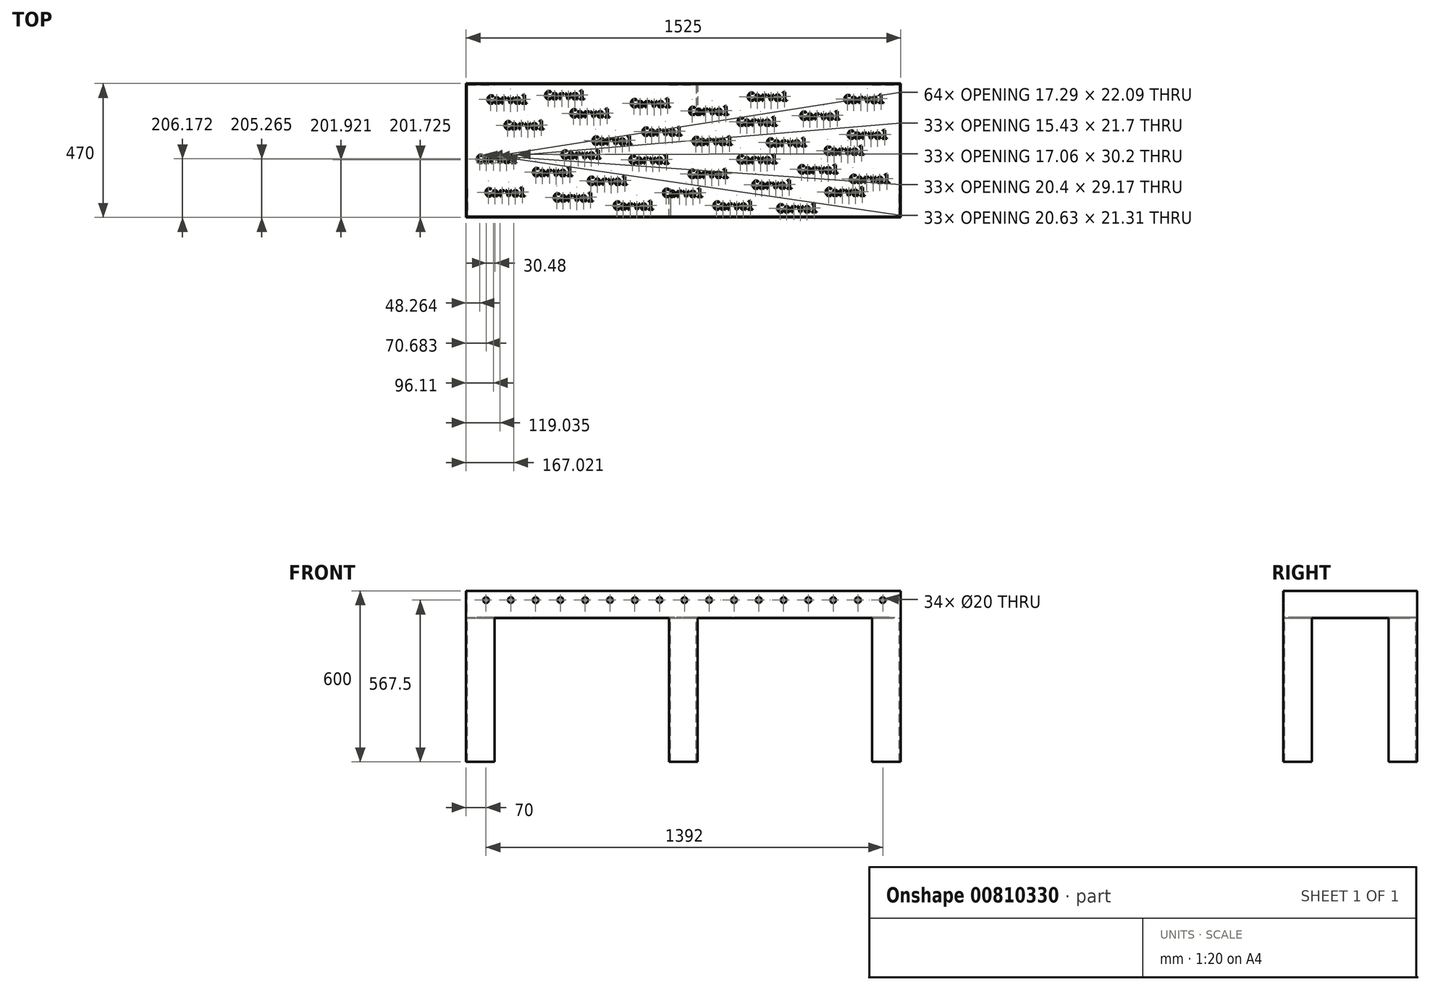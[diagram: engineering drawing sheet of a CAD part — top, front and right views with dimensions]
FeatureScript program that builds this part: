
annotation { "Feature Type Name" : "Feature", "Feature Type Description" : "" }
export const myFeature = defineFeature(function(context is Context, id is Id, definition is map)
    precondition{}
    {
        {
            var Q0;
            Q0=qCreatedBy(makeId("Top.planeOp"),FACE);
            var sketch = newSketch(context, id + "F0", { "sketchPlane" : qUnion([Q0])});
            skLineSegment(sketch, "E0.bottom", {"start": v(-762.5, 235) * mm, "end": v(762.5, 235) * mm});
            skLineSegment(sketch, "E0.top", {"start": v(-762.5, -235) * mm, "end": v(762.5, -235) * mm});
            skLineSegment(sketch, "E0.left", {"start": v(-762.5, 235) * mm, "end": v(-762.5, -235) * mm});
            skLineSegment(sketch, "E0.right", {"start": v(762.5, 235) * mm, "end": v(762.5, -235) * mm});
            skLineSegment(sketch, "E1", {"start": v(0, 856.04) * mm, "end": v(0, -701.59) * mm, "construction": true});
            skLineSegment(sketch, "E2", {"start": v(-980.05, 0) * mm, "end": v(1795.85, 0) * mm, "construction": true});
            skSolve(sketch);
        }
        {
            var Q0;
            Q0 = qSketchRegion(id + "F0", true);
            extrude(context, id + "F1", {"entities" : qUnion([Q0]), "depth" : 125 * mm, "offsetDistance" : 25.4 * mm});
        }
        {
            var Q0;
            Q0=makeQuery(id+"F1.opExtrude","CAP_FACE",FACE,{"disambiguationData":[OSD([sQuery(id+"F0.wireOp",EDGE,"E0.bottom"),sQuery(id+"F0.wireOp",EDGE,"E0.top"),sQuery(id+"F0.wireOp",EDGE,"E0.left"),sQuery(id+"F0.wireOp",EDGE,"E0.right")])],"isStart":false});
            shell(context, id + "F2", {"entities" : qUnion([Q0]), "thickness" : 2.54 * mm});
        }
        {
            var Q0;
            Q0=makeQuery(id+"F2.opShell","OFFSET_FACE",FACE,{"disambiguationData":[OSD([sQuery(id+"F0.wireOp",EDGE,"E0.bottom"),sQuery(id+"F0.wireOp",EDGE,"E0.top"),sQuery(id+"F0.wireOp",EDGE,"E0.left"),sQuery(id+"F0.wireOp",EDGE,"E0.right")])]});
            var sketch = newSketch(context, id + "F3", { "sketchPlane" : qUnion([Q0])});
            skText(sketch, "E3", { "text": "Carval", "fontName": "DroidSansMono.ttf"});
            skText(sketch, "E4", { "text": "Carval", "fontName": "DroidSansMono.ttf"});
            skText(sketch, "E5", { "text": "Carval", "fontName": "DroidSansMono.ttf"});
            skText(sketch, "E6", { "text": "Carval", "fontName": "DroidSansMono.ttf"});
            skText(sketch, "E7", { "text": "Carval", "fontName": "DroidSansMono.ttf"});
            skText(sketch, "E8", { "text": "Carval", "fontName": "DroidSansMono.ttf"});
            skText(sketch, "E9", { "text": "Carval", "fontName": "DroidSansMono.ttf"});
            skText(sketch, "E10", { "text": "Carval", "fontName": "DroidSansMono.ttf"});
            skText(sketch, "E11", { "text": "Carval", "fontName": "DroidSansMono.ttf"});
            skText(sketch, "E12", { "text": "Carval", "fontName": "DroidSansMono.ttf"});
            skText(sketch, "E13", { "text": "Carval", "fontName": "DroidSansMono.ttf"});
            skText(sketch, "E14", { "text": "Carval", "fontName": "DroidSansMono.ttf"});
            skText(sketch, "E15", { "text": "Carval", "fontName": "DroidSansMono.ttf"});
            skText(sketch, "E16", { "text": "Carval", "fontName": "DroidSansMono.ttf"});
            skText(sketch, "E17", { "text": "Carval", "fontName": "DroidSansMono.ttf"});
            skText(sketch, "E18", { "text": "Carval", "fontName": "DroidSansMono.ttf"});
            skText(sketch, "E19", { "text": "Carval", "fontName": "DroidSansMono.ttf"});
            skText(sketch, "E20", { "text": "Carval", "fontName": "DroidSansMono.ttf"});
            skText(sketch, "E21", { "text": "Carval", "fontName": "DroidSansMono.ttf"});
            skText(sketch, "E22", { "text": "Carval", "fontName": "DroidSansMono.ttf"});
            skText(sketch, "E23", { "text": "Carval", "fontName": "DroidSansMono.ttf"});
            skText(sketch, "E24", { "text": "Carval", "fontName": "DroidSansMono.ttf"});
            skText(sketch, "E25", { "text": "Carval", "fontName": "DroidSansMono.ttf"});
            skText(sketch, "E26", { "text": "Carval", "fontName": "DroidSansMono.ttf"});
            skText(sketch, "E27", { "text": "Carval", "fontName": "DroidSansMono.ttf"});
            skText(sketch, "E28", { "text": "Carval", "fontName": "DroidSansMono.ttf"});
            skText(sketch, "E29", { "text": "Carval", "fontName": "DroidSansMono.ttf"});
            skText(sketch, "E30", { "text": "Carval", "fontName": "DroidSansMono.ttf"});
            skText(sketch, "E31", { "text": "Carval", "fontName": "DroidSansMono.ttf"});
            skText(sketch, "E32", { "text": "Carval", "fontName": "DroidSansMono.ttf"});
            skText(sketch, "E33", { "text": "Carval", "fontName": "DroidSansMono.ttf"});
            skText(sketch, "E34", { "text": "Carval", "fontName": "DroidSansMono.ttf"});
            skText(sketch, "E35", { "text": "Carval", "fontName": "DroidSansMono.ttf"});
            const initialGuessF3  = {"E3": [-0.68963, 0.16459, 1, 0, 0.02862], "E4": [-0.42989, -0.02862, 1, 0, 0.02862], "E5": [-0.62965, 0.07406, 1, 0, 0.02862], "E6": [0.18749, -0.04564, 1, 0, 0.02862], "E7": [0.18749, 0.08636, 1, 0, 0.02862], "E8": [-0.33727, -0.1208, 1, 0, 0.02862], "E9": [-0.07385, -0.16299, 1, 0, 0.02862], "E10": [-0.39859, 0.11611, 1, 0, 0.02862], "E11": [-0.14618, 0.05183, 1, 0, 0.02862], "E12": [-0.19132, -0.04647, 1, 0, 0.02862], "E13": [-0.72694, -0.04393, 1, 0, 0.02862], "E14": [-0.69646, -0.16134, 1, 0, 0.02862], "E15": [-0.53019, -0.09022, 1, 0, 0.02862], "E16": [-0.45721, -0.17912, 1, 0, 0.02862], "E17": [-0.1866, 0.15167, 1, 0, 0.02862], "E18": [0.03048, 0.0188, 1, 0, 0.02862], "E19": [-0.32135, 0.02032, 1, 0, 0.02862], "E20": [-0.24638, -0.20756, 1, 0, 0.02862], "E21": [0.01622, -0.09626, 1, 0, 0.02862], "E22": [0.01778, 0.12446, 1, 0, 0.02862], "E23": [0.29106, 0.01376, 1, 0, 0.02862], "E24": [0.10343, -0.20743, 1, 0, 0.02862], "E25": [-0.48735, 0.17962, 1, 0, 0.02862], "E26": [0.22369, 0.17436, 1, 0, 0.02862], "E27": [0.24015, -0.13454, 1, 0, 0.02862], "E28": [0.4081, 0.10772, 1, 0, 0.02862], "E29": [0.40134, -0.08052, 1, 0, 0.02862], "E30": [0.32725, -0.21722, 1, 0, 0.02862], "E31": [0.49366, -0.01524, 1, 0, 0.02862], "E32": [0.49669, -0.15994, 1, 0, 0.02862], "E33": [0.56243, 0.16614, 1, 0, 0.02862], "E34": [0.57453, 0.04132, 1, 0, 0.02862], "E35": [0.58236, -0.11424, 1, 0, 0.02862]};
            skSetInitialGuess(sketch, initialGuessF3);
            skSolve(sketch);
        }
        {
            var Q0;
            Q0 = qSketchRegion(id + "F3", true);
            extrude(context, id + "F4", {"entities" : qUnion([Q0]), "operationType" : NewBodyOperationType.REMOVE, "endBound" : BoundingType.UP_TO_NEXT, "oppositeDirection" : true, "depth" : 25.4 * mm, "offsetDistance" : 25.4 * mm});
        }
        {
            var Q0;
            Q0=makeQuery(id+"F1.opExtrude","SWEPT_FACE",FACE,{"disambiguationData":[OSD([sQuery(id+"F0.wireOp",EDGE,"E0.top")])]});
            var sketch = newSketch(context, id + "F5", { "sketchPlane" : qUnion([Q0])});
            skLineSegment(sketch, "E36", {"start": v(-881.57, 62.5) * mm, "end": v(843.19, 62.5) * mm, "construction": true});
            skPoint(sketch, "E36.startSnap0", {"position": v(-762.5, 62.5) * mm});
            skCircle(sketch, "E37", {"center": v(-692.5, 62.5) * mm, "radius": 10 * mm});
            skCircle(sketch, "E38.1.0.0", {"center": v(-605.5, 62.5) * mm, "radius": 10 * mm});
            skCircle(sketch, "E38.2.0.0", {"center": v(-518.5, 62.5) * mm, "radius": 10 * mm});
            skCircle(sketch, "E38.3.0.0", {"center": v(-431.5, 62.5) * mm, "radius": 10 * mm});
            skCircle(sketch, "E38.4.0.0", {"center": v(-344.5, 62.5) * mm, "radius": 10 * mm});
            skCircle(sketch, "E38.5.0.0", {"center": v(-257.5, 62.5) * mm, "radius": 10 * mm});
            skCircle(sketch, "E38.6.0.0", {"center": v(-170.5, 62.5) * mm, "radius": 10 * mm});
            skCircle(sketch, "E38.7.0.0", {"center": v(-83.5, 62.5) * mm, "radius": 10 * mm});
            skCircle(sketch, "E38.8.0.0", {"center": v(3.5, 62.5) * mm, "radius": 10 * mm});
            skCircle(sketch, "E38.9.0.0", {"center": v(90.5, 62.5) * mm, "radius": 10 * mm});
            skCircle(sketch, "E38.10.0.0", {"center": v(177.5, 62.5) * mm, "radius": 10 * mm});
            skCircle(sketch, "E38.11.0.0", {"center": v(264.5, 62.5) * mm, "radius": 10 * mm});
            skCircle(sketch, "E38.12.0.0", {"center": v(351.5, 62.5) * mm, "radius": 10 * mm});
            skCircle(sketch, "E38.13.0.0", {"center": v(438.5, 62.5) * mm, "radius": 10 * mm});
            skLineSegment(sketch, "E38.direction1", {"start": v(-692.5, 62.5) * mm, "end": v(-605.5, 62.5) * mm, "construction": true});
            skCircle(sketch, "E39.0.14.0", {"center": v(525.5, 62.5) * mm, "radius": 10 * mm});
            skCircle(sketch, "E39.0.15.0", {"center": v(612.5, 62.5) * mm, "radius": 10 * mm});
            skCircle(sketch, "E39.0.16.0", {"center": v(699.5, 62.5) * mm, "radius": 10 * mm});
            skSolve(sketch);
        }
        {
            var Q0;
            Q0 = qSketchRegion(id + "F5", true);
            extrude(context, id + "F6", {"entities" : qUnion([Q0]), "operationType" : NewBodyOperationType.REMOVE, "endBound" : BoundingType.THROUGH_ALL, "oppositeDirection" : true, "depth" : 25.4 * mm, "offsetDistance" : 25.4 * mm});
        }
        {
            var Q0;
            {var subQ0=sQuery(id+"F0.wireOp",EDGE,"E0.left");var subQ1=sQuery(id+"F0.wireOp",EDGE,"E0.top");var subQ2=sQuery(id+"F0.wireOp",EDGE,"E0.right");var subQ3=sQuery(id+"F0.wireOp",EDGE,"E0.bottom");Q0=makeQuery(id+"F4.boolean.opBoolean","SPLIT",FACE,{"disambiguationData":[TD([makeQuery(id+"F1.opExtrude","SWEPT_FACE",FACE,{"disambiguationData":[OSD([subQ3])]})])],"derivedFrom":makeQuery(id+"F1.opExtrude","CAP_FACE",FACE,{"disambiguationData":[OSD([subQ3,subQ1,subQ0,subQ2])],"isStart":true})});}
            var sketch = newSketch(context, id + "F7", { "sketchPlane" : qUnion([Q0])});
            skLineSegment(sketch, "E40", {"start": v(-762.5, 235) * mm, "end": v(-762.5, 135) * mm});
            skLineSegment(sketch, "E41", {"start": v(-757.5, 135) * mm, "end": v(-757.5, 230) * mm});
            skLineSegment(sketch, "E42", {"start": v(-757.5, 230) * mm, "end": v(-662.5, 230) * mm});
            skLineSegment(sketch, "E43", {"start": v(-662.5, 230) * mm, "end": v(-662.5, 235) * mm});
            skLineSegment(sketch, "E44", {"start": v(-662.5, 235) * mm, "end": v(-762.5, 235) * mm});
            skLineSegment(sketch, "E45", {"start": v(-762.5, 135) * mm, "end": v(-757.5, 135) * mm});
            skLineSegment(sketch, "E46", {"start": v(-762.5, -235) * mm, "end": v(-762.5, -135) * mm});
            skLineSegment(sketch, "E47", {"start": v(-757.5, -230) * mm, "end": v(-662.5, -230) * mm});
            skLineSegment(sketch, "E48", {"start": v(-662.5, -230) * mm, "end": v(-662.5, -235) * mm});
            skLineSegment(sketch, "E49", {"start": v(-662.5, -235) * mm, "end": v(-662.5, -235) * mm});
            skLineSegment(sketch, "E50", {"start": v(-662.5, -235) * mm, "end": v(-762.5, -235) * mm});
            skLineSegment(sketch, "E51", {"start": v(-762.5, -135) * mm, "end": v(-757.5, -135) * mm});
            skLineSegment(sketch, "E52", {"start": v(-757.5, -135) * mm, "end": v(-757.5, -230) * mm});
            skLineSegment(sketch, "E53", {"start": v(0, 378.86) * mm, "end": v(0, -304.4) * mm, "construction": true});
            skPoint(sketch, "E53.endSnap0", {"position": v(0, -235) * mm});
            skLineSegment(sketch, "E54", {"start": v(50, 235) * mm, "end": v(-50, 235) * mm});
            skLineSegment(sketch, "E55", {"start": v(-50, 235) * mm, "end": v(-50, 135) * mm});
            skLineSegment(sketch, "E56", {"start": v(-50, 135) * mm, "end": v(-45, 135) * mm});
            skLineSegment(sketch, "E57", {"start": v(-45, 135) * mm, "end": v(-45, 230) * mm});
            skLineSegment(sketch, "E58", {"start": v(-45, 230) * mm, "end": v(50, 230) * mm});
            skLineSegment(sketch, "E59", {"start": v(50, 230) * mm, "end": v(50, 235) * mm});
            skLineSegment(sketch, "E60", {"start": v(-50, -235) * mm, "end": v(50, -235) * mm});
            skLineSegment(sketch, "E61", {"start": v(50, -235) * mm, "end": v(50, -135) * mm});
            skLineSegment(sketch, "E62", {"start": v(-50, -235) * mm, "end": v(-50, -230) * mm});
            skLineSegment(sketch, "E63", {"start": v(-50, -230) * mm, "end": v(45, -230) * mm});
            skLineSegment(sketch, "E64", {"start": v(45, -230) * mm, "end": v(45, -135) * mm});
            skLineSegment(sketch, "E65", {"start": v(45, -135) * mm, "end": v(50, -135) * mm});
            skLineSegment(sketch, "E66", {"start": v(762.5, 235) * mm, "end": v(662.5, 235) * mm});
            skLineSegment(sketch, "E67", {"start": v(762.5, 235) * mm, "end": v(762.5, 135) * mm});
            skLineSegment(sketch, "E68", {"start": v(662.5, 235) * mm, "end": v(662.5, 230) * mm});
            skLineSegment(sketch, "E69", {"start": v(662.5, 230) * mm, "end": v(757.5, 230) * mm});
            skLineSegment(sketch, "E70", {"start": v(757.5, 230) * mm, "end": v(757.5, 135) * mm});
            skLineSegment(sketch, "E71", {"start": v(757.5, 135) * mm, "end": v(762.5, 135) * mm});
            skLineSegment(sketch, "E72", {"start": v(762.5, -135) * mm, "end": v(762.5, -235) * mm});
            skLineSegment(sketch, "E73", {"start": v(762.5, -235) * mm, "end": v(662.5, -235) * mm});
            skLineSegment(sketch, "E74", {"start": v(662.5, -235) * mm, "end": v(662.5, -230) * mm});
            skLineSegment(sketch, "E75", {"start": v(662.5, -230) * mm, "end": v(757.5, -230) * mm});
            skLineSegment(sketch, "E76", {"start": v(757.5, -230) * mm, "end": v(757.5, -135) * mm});
            skLineSegment(sketch, "E77", {"start": v(757.5, -135) * mm, "end": v(762.5, -135) * mm});
            skSolve(sketch);
        }
        {
            var Q0;
            Q0 = qSketchRegion(id + "F7", true);
            extrude(context, id + "F8", {"entities" : qUnion([Q0]), "operationType" : NewBodyOperationType.ADD, "depth" : 505 * mm, "offsetDistance" : 25.4 * mm});
        }
        {
            var Q0;
            Q0=makeQuery(id+"F8.boolean.opBoolean","MERGE",FACE,{"derivedFrom":[makeQuery(id+"F1.opExtrude","SWEPT_FACE",FACE,{"disambiguationData":[OSD([sQuery(id+"F0.wireOp",EDGE,"E0.right")])]}),makeQuery(id+"F8.opExtrude","SWEPT_FACE",FACE,{"disambiguationData":[OSD([sQuery(id+"F7.wireOp",EDGE,"E67")])]}),makeQuery(id+"F8.opExtrude","SWEPT_FACE",FACE,{"disambiguationData":[OSD([sQuery(id+"F7.wireOp",EDGE,"E72")])]})]});
            var sketch = newSketch(context, id + "F9", { "sketchPlane" : qUnion([Q0])});
            skLineSegment(sketch, "E78.bottom", {"start": v(-269.37, 125) * mm, "end": v(260.82, 125) * mm});
            skLineSegment(sketch, "E78.top", {"start": v(-269.37, 95) * mm, "end": v(260.82, 95) * mm});
            skLineSegment(sketch, "E78.left", {"start": v(-269.37, 125) * mm, "end": v(-269.37, 95) * mm});
            skLineSegment(sketch, "E78.right", {"start": v(260.82, 125) * mm, "end": v(260.82, 95) * mm});
            skSolve(sketch);
        }
        {
            var Q0;
            Q0 = qSketchRegion(id + "F9", true);
            extrude(context, id + "F10", {"entities" : qUnion([Q0]), "operationType" : NewBodyOperationType.REMOVE, "endBound" : BoundingType.THROUGH_ALL, "oppositeDirection" : true, "depth" : 25.4 * mm, "offsetDistance" : 25.4 * mm});
        }
    });
